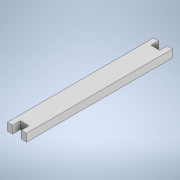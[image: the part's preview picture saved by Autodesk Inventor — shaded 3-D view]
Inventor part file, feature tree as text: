
AUTODESK INVENTOR PART (.ipt)
format: ipt  version: 2020 (Build 240168000, 168)  size: 107,008 bytes
history: native  units: mm
features: extrude x1, sketch x1
ambient origin geometry x8: Origin, YZ Plane, XZ Plane, XY Plane, X Axis, Y Axis, Z Axis, Center Point
bodies: Solide1 (feature_tree)
feature tree (2):
  extrude  "Extrusion1"  Depth=419.0mm
  sketch  "Esquisse1"
